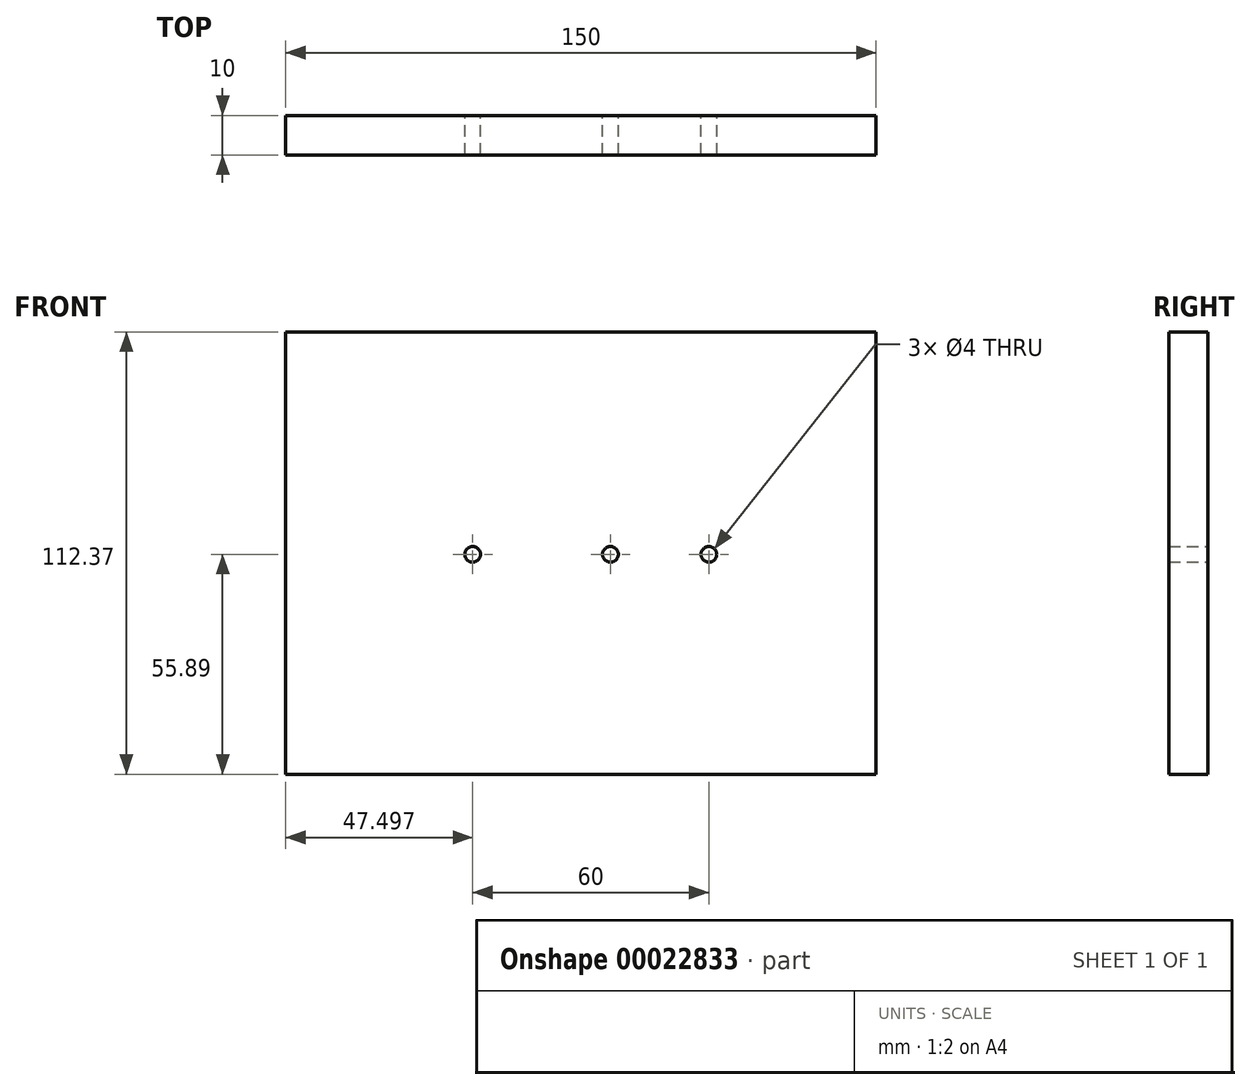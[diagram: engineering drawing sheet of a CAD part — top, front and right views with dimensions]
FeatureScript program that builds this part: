
annotation { "Feature Type Name" : "Feature", "Feature Type Description" : "" }
export const myFeature = defineFeature(function(context is Context, id is Id, definition is map)
    precondition{}
    {
        {
            var Q0;
            Q0=qCreatedBy(makeId("Front.planeOp"),FACE);
            var sketch = newSketch(context, id + "F0", { "sketchPlane" : qUnion([Q0])});
            skLineSegment(sketch, "E0.bottom", {"start": v(-99.85, 56.48) * mm, "end": v(50.15, 56.48) * mm});
            skLineSegment(sketch, "E0.top", {"start": v(-99.85, -55.9) * mm, "end": v(50.15, -55.9) * mm});
            skLineSegment(sketch, "E0.left", {"start": v(-99.85, 56.48) * mm, "end": v(-99.85, -55.9) * mm});
            skLineSegment(sketch, "E0.right", {"start": v(50.15, 56.48) * mm, "end": v(50.15, -55.9) * mm});
            skCircle(sketch, "E1", {"center": v(-52.35, 0) * mm, "radius": 2 * mm});
            skCircle(sketch, "E2", {"center": v(-17.35, 0) * mm, "radius": 2 * mm});
            skCircle(sketch, "E3", {"center": v(7.65, 0) * mm, "radius": 2 * mm});
            skSolve(sketch);
        }
        {
            var Q0;
            Q0=makeQuery(id+"F0.imprint","IMPRINT",FACE,{"disambiguationData":[TD([[makeQuery(id+"F0.imprint","IMPRINT",EDGE,{"derivedFrom":sQuery(id+"F0.wireOp",EDGE,"E0.bottom")}),-1.0]])]});
            extrude(context, id + "F1", {"entities" : qUnion([Q0]), "depth" : 10 * mm});
        }
    });
